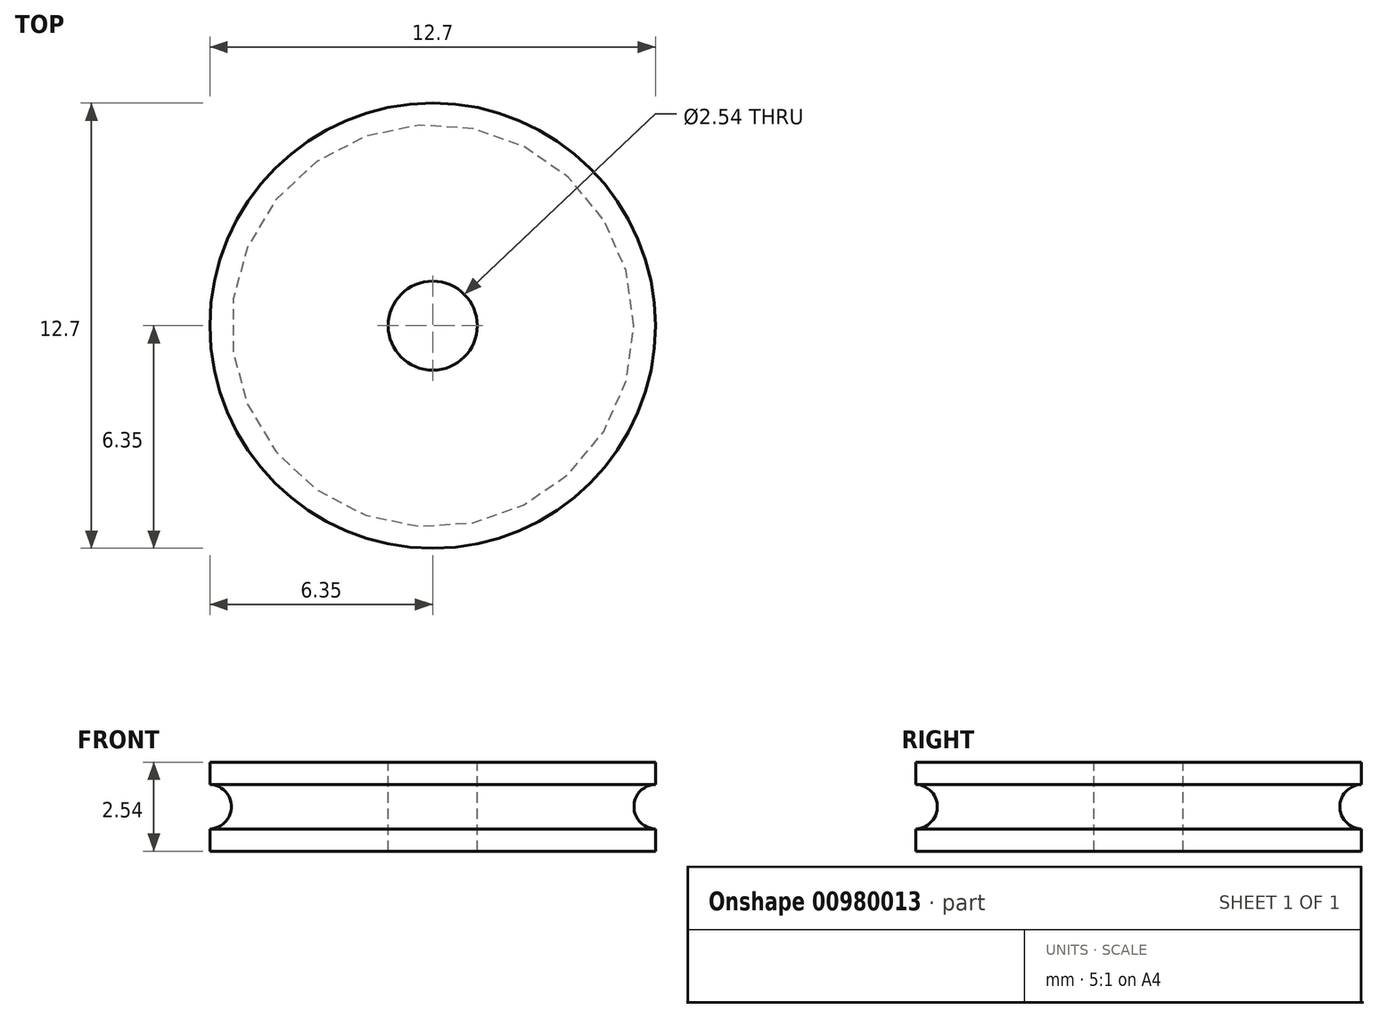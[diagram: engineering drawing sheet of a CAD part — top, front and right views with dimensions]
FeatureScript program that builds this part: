
annotation { "Feature Type Name" : "Feature", "Feature Type Description" : "" }
export const myFeature = defineFeature(function(context is Context, id is Id, definition is map)
    precondition{}
    {
        {
            var Q0;
            Q0=qCreatedBy(makeId("Top.planeOp"),FACE);
            var sketch = newSketch(context, id + "F0", { "sketchPlane" : qUnion([Q0])});
            skCircle(sketch, "E0", {"center": v(0, 0) * mm, "radius": 6.35 * mm});
            skSolve(sketch);
        }
        {
            var Q0;
            Q0=qSketchRegion(id+"F0",true);
            extrude(context, id + "F1", {"entities" : qUnion([Q0]), "depth" : 2.54 * mm, "offsetDistance" : 25.4 * mm});
        }
        {
            var Q0;
            Q0=qCreatedBy(makeId("Front.planeOp"),FACE);
            var sketch = newSketch(context, id + "F2", { "sketchPlane" : qUnion([Q0])});
            skCircle(sketch, "E1", {"center": v(-6.37, 1.27) * mm, "radius": 0.64 * mm});
            skSolve(sketch);
        }
        {
            var Q0;
            Q0=makeQuery(id+"F2.imprint","IMPRINT",FACE,{"disambiguationData":[TD([[makeQuery(id+"F2.imprint","IMPRINT",EDGE,{"derivedFrom":sQuery(id+"F2.wireOp",EDGE,"E1")}),1.0]])]});
            var Q1;
            Q1=makeQuery(id+"F1.opExtrude","CAP_EDGE",EDGE,{"disambiguationData":[OSD([sQuery(id+"F0.wireOp",EDGE,"E0")])],"isStart":false});
            revolve(context, id + "F3", {"operationType" : NewBodyOperationType.REMOVE, "surfaceOperationType" : NewSurfaceOperationType.NEW, "entities" : qUnion([Q0]), "axis" : qUnion([Q1]), "revolveType" : RevolveType.FULL, "oppositeDirection" : true});
        }
        {
            var Q0;
            Q0=makeQuery(id+"F1.opExtrude","CAP_FACE",FACE,{"disambiguationData":[OSD([sQuery(id+"F0.wireOp",EDGE,"E0")])],"isStart":false});
            var sketch = newSketch(context, id + "F4", { "sketchPlane" : qUnion([Q0])});
            skCircle(sketch, "E2", {"center": v(0, 0) * mm, "radius": 1.27 * mm});
            skSolve(sketch);
        }
        {
            var Q0;
            Q0=qSketchRegion(id+"F4",true);
            extrude(context, id + "F5", {"entities" : qUnion([Q0]), "operationType" : NewBodyOperationType.REMOVE, "oppositeDirection" : true, "depth" : 2.54 * mm, "offsetDistance" : 25.4 * mm});
        }
    });
